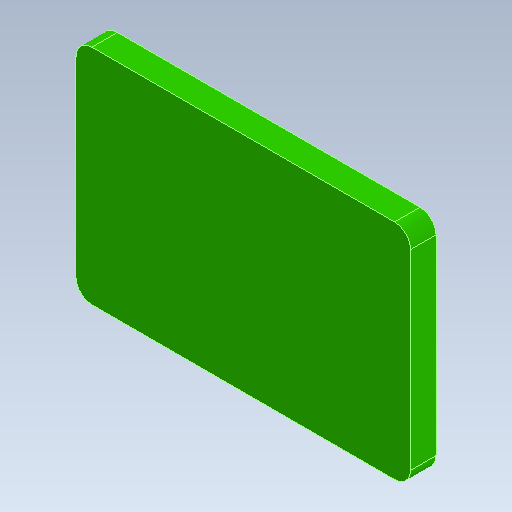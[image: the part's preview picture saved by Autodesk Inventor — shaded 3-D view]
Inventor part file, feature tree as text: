
AUTODESK INVENTOR PART (.ipt)
format: ipt  version: 2021 (Build 250183000, 183)  size: 120,320 bytes
history: native  units: mm
features: reference x8, other x4, extrude x1, fillet x1, sketch x1, projected_geometry x1
ambient origin geometry x8: Origin, YZ Plane, XZ Plane, XY Plane, X Axis, Y Axis, Z Axis, Center Point
bodies: Solid1 (feature_tree)
feature tree (16):
  extrude  "Extrusion1"  Depth=14.0mm
  fillet  "Fillet1"  Radius=1.6mm
  other  "HDMI_ADAPTER_PCB_OUTLINE"
  sketch  "Sketch1"  dims[d0=21.0mm d1=14.0mm d2=1.6mm d3=0.0mm d4=1.0mm d5=0.3mm d6=0.15mm d7=0.15mm]
  reference  "Reference2"
  reference  "Reference3"
  reference  "Reference4"
  reference  "Reference5"
  reference  "Reference6"
  reference  "Reference7"
  reference  "Reference8"
  reference  "Reference9"
  projected_geometry  "Projected Loop1"
  other  "<userpath>\Google Drive\Unicorn 2020\CAD\Assembly.iam"
  other  "Assembly.iam"
  other  "MHDRA511M0:3"
